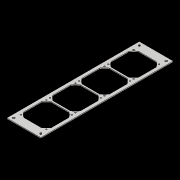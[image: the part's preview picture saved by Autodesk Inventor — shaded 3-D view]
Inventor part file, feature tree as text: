
AUTODESK INVENTOR PART (.ipt)
format: ipt  version: 2018.2 (Build 222227000, 227)  size: 217,088 bytes
history: native  units: mm
features: extrude x2, sketch x2, other x1
ambient origin geometry x8: Origin, YZ Plane, XZ Plane, XY Plane, X Axis, Y Axis, Z Axis, Center Point
bodies: Body1 (feature_tree)
feature tree (5):
  other  "ソリッド1"
  extrude  "押し出し1"  Depth=110.0mm
  extrude  "押し出し2"  Depth=430.0mm
  sketch  "スケッチ1"
  sketch  "スケッチ2"
